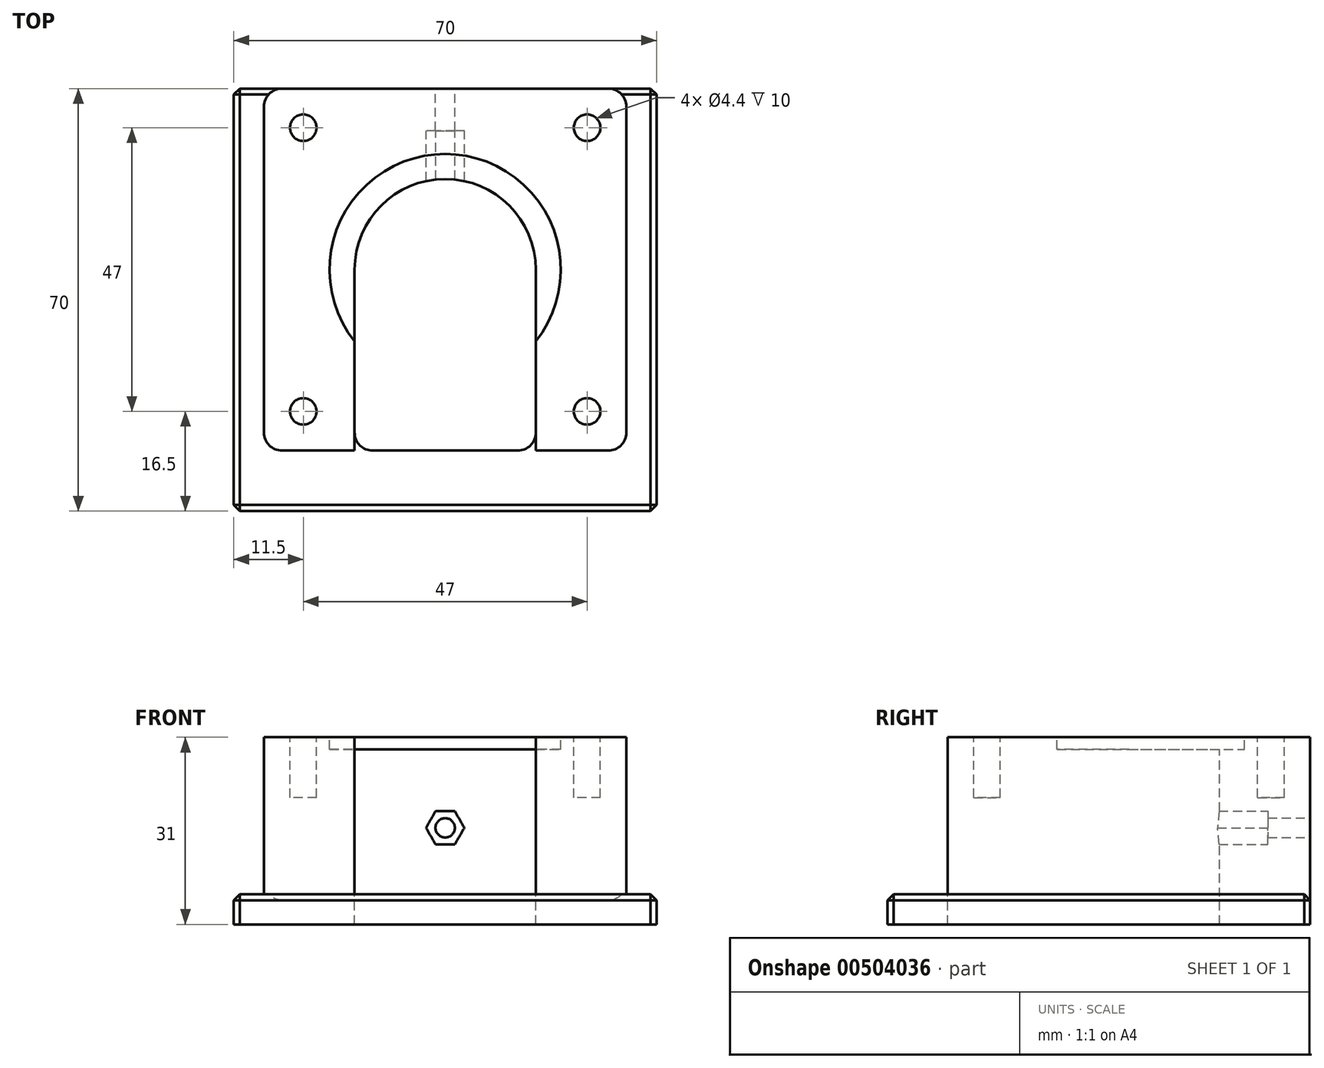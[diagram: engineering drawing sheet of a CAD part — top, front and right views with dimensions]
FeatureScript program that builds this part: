
annotation { "Feature Type Name" : "Feature", "Feature Type Description" : "" }
export const myFeature = defineFeature(function(context is Context, id is Id, definition is map)
    precondition{}
    {
        {
            var Q0;
            Q0=qCreatedBy(makeId("Top.planeOp"),FACE);
            var sketch = newSketch(context, id + "F0", { "sketchPlane" : qUnion([Q0])});
            skLineSegment(sketch, "E0.bottom", {"start": v(35, -35) * mm, "end": v(-35, -35) * mm});
            skLineSegment(sketch, "E0.top", {"start": v(35, 35) * mm, "end": v(-35, 35) * mm});
            skLineSegment(sketch, "E0.left", {"start": v(35, -35) * mm, "end": v(35, 35) * mm});
            skLineSegment(sketch, "E0.right", {"start": v(-35, -35) * mm, "end": v(-35, 35) * mm});
            skPoint(sketch, "E0.middle", {"position": v(0, 0) * mm});
            skSolve(sketch);
        }
        {
            var Q0;
            Q0=makeQuery(id+"F0.imprint","IMPRINT",FACE,{"disambiguationData":[TD([[makeQuery(id+"F0.imprint","IMPRINT",EDGE,{"derivedFrom":sQuery(id+"F0.wireOp",EDGE,"E0.bottom")}),-1.0]])]});
            extrude(context, id + "F1", {"entities" : qUnion([Q0]), "depth" : 5 * mm});
        }
        {
            var Q0;
            Q0=makeQuery(id+"F1.opExtrude","CAP_FACE",FACE,{"disambiguationData":[OSD([sQuery(id+"F0.wireOp",EDGE,"E0.bottom"),sQuery(id+"F0.wireOp",EDGE,"E0.top"),sQuery(id+"F0.wireOp",EDGE,"E0.left"),sQuery(id+"F0.wireOp",EDGE,"E0.right")])],"isStart":false});
            var sketch = newSketch(context, id + "F2", { "sketchPlane" : qUnion([Q0])});
            skLineSegment(sketch, "E1.bottom", {"start": v(30, -25) * mm, "end": v(-30, -25) * mm});
            skLineSegment(sketch, "E1.top", {"start": v(30, 35) * mm, "end": v(-30, 35) * mm});
            skLineSegment(sketch, "E1.left", {"start": v(30, -25) * mm, "end": v(30, 35) * mm});
            skLineSegment(sketch, "E1.right", {"start": v(-30, -25) * mm, "end": v(-30, 35) * mm});
            skPoint(sketch, "E1.middle", {"position": v(0, 5) * mm});
            skPoint(sketch, "E2", {"position": v(0, 35) * mm});
            skSolve(sketch);
        }
        {
            var Q0;
            Q0=makeQuery(id+"F2.imprint","IMPRINT",FACE,{"disambiguationData":[TD([[makeQuery(id+"F2.imprint","IMPRINT",EDGE,{"derivedFrom":sQuery(id+"F2.wireOp",EDGE,"E1.bottom")}),-1.0]])]});
            extrude(context, id + "F3", {"entities" : qUnion([Q0]), "operationType" : NewBodyOperationType.ADD, "depth" : 26 * mm});
        }
        {
            var Q0;
            Q0=makeQuery(id+"F3.opExtrude","CAP_FACE",FACE,{"disambiguationData":[OSD([sQuery(id+"F2.wireOp",EDGE,"E1.bottom"),sQuery(id+"F2.wireOp",EDGE,"E1.top"),sQuery(id+"F2.wireOp",EDGE,"E1.left"),sQuery(id+"F2.wireOp",EDGE,"E1.right")])],"isStart":false});
            var sketch = newSketch(context, id + "F4", { "sketchPlane" : qUnion([Q0])});
            skLineSegment(sketch, "E3.bottom", {"start": v(23.5, -18.5) * mm, "end": v(-23.5, -18.5) * mm, "construction": true});
            skLineSegment(sketch, "E3.top", {"start": v(23.5, 28.5) * mm, "end": v(-23.5, 28.5) * mm, "construction": true});
            skLineSegment(sketch, "E3.left", {"start": v(23.5, -18.5) * mm, "end": v(23.5, 28.5) * mm, "construction": true});
            skLineSegment(sketch, "E3.right", {"start": v(-23.5, -18.5) * mm, "end": v(-23.5, 28.5) * mm, "construction": true});
            skCircle(sketch, "E4", {"center": v(-23.5, 28.5) * mm, "radius": 2.2 * mm});
            skCircle(sketch, "E5", {"center": v(23.5, 28.5) * mm, "radius": 2.2 * mm});
            skCircle(sketch, "E6", {"center": v(-23.5, -18.5) * mm, "radius": 2.2 * mm});
            skCircle(sketch, "E7", {"center": v(23.5, -18.5) * mm, "radius": 2.2 * mm});
            skCircle(sketch, "E8", {"center": v(0, 5) * mm, "radius": 15 * mm});
            skLineSegment(sketch, "E9", {"start": v(-23.5, 28.5) * mm, "end": v(23.5, -18.5) * mm, "construction": true});
            skLineSegment(sketch, "E10", {"start": v(23.5, 28.5) * mm, "end": v(-23.5, -18.5) * mm, "construction": true});
            skLineSegment(sketch, "E11", {"start": v(15, 5) * mm, "end": v(15, -25) * mm});
            skLineSegment(sketch, "E12", {"start": v(-15, 5) * mm, "end": v(-15, -25) * mm});
            skLineSegment(sketch, "E13", {"start": v(-30, 35) * mm, "end": v(30, -25) * mm, "construction": true});
            skLineSegment(sketch, "E14", {"start": v(30, 35) * mm, "end": v(-30, -25) * mm, "construction": true});
            skCircle(sketch, "E15", {"center": v(0, 5) * mm, "radius": 19.15 * mm});
            skSolve(sketch);
        }
        {
            var Q0;
            Q0=makeQuery(id+"F4.imprint","IMPRINT",FACE,{"disambiguationData":[TD([[makeQuery(id+"F4.imprint","IMPRINT",EDGE,{"derivedFrom":sQuery(id+"F4.wireOp",EDGE,"E6")}),1.0]])]});
            var Q1;
            Q1=makeQuery(id+"F4.imprint","IMPRINT",FACE,{"disambiguationData":[TD([[makeQuery(id+"F4.imprint","IMPRINT",EDGE,{"derivedFrom":sQuery(id+"F4.wireOp",EDGE,"E4")}),1.0]])]});
            var Q2;
            Q2=makeQuery(id+"F4.imprint","IMPRINT",FACE,{"disambiguationData":[TD([[makeQuery(id+"F4.imprint","IMPRINT",EDGE,{"derivedFrom":sQuery(id+"F4.wireOp",EDGE,"E5")}),1.0]])]});
            var Q3;
            Q3=makeQuery(id+"F4.imprint","IMPRINT",FACE,{"disambiguationData":[TD([[makeQuery(id+"F4.imprint","IMPRINT",EDGE,{"derivedFrom":sQuery(id+"F4.wireOp",EDGE,"E7")}),1.0]])]});
            var Q4;
            Q4=makeQuery(id+"F1.opExtrude","CAP_FACE",FACE,{"disambiguationData":[OSD([sQuery(id+"F0.wireOp",EDGE,"E0.bottom"),sQuery(id+"F0.wireOp",EDGE,"E0.top"),sQuery(id+"F0.wireOp",EDGE,"E0.left"),sQuery(id+"F0.wireOp",EDGE,"E0.right")])],"isStart":true});
            extrude(context, id + "F5", {"entities" : qUnion([Q0, Q1, Q2, Q3]), "operationType" : NewBodyOperationType.REMOVE, "oppositeDirection" : true, "endBoundEntityFace" : qUnion([Q4]), "offsetDistance" : 25 * mm, "depth" : 10 * mm});
        }
        {
            var Q0;
            {var subQ0=sQuery(id+"F4.wireOp",EDGE,"E8");var subQ1=makeQuery(id+"F4.imprint","INTERSECT",VERTEX,{"derivedFrom":[subQ0,sQuery(id+"F4.wireOp",EDGE,"E11")]});Q0=makeQuery(id+"F4.imprint","IMPRINT",FACE,{"disambiguationData":[TD([[makeQuery(id+"F4.imprint","IMPRINT",EDGE,{"disambiguationData":[TD([[subQ1,-1.0]])],"derivedFrom":subQ0}),1.0]])]});}
            var Q1;
            {var subQ0=sQuery(id+"F4.wireOp",EDGE,"E11");var subQ1=sQuery(id+"F4.wireOp",EDGE,"E8");var subQ2=makeQuery(id+"F4.imprint","INTERSECT",VERTEX,{"derivedFrom":[subQ1,subQ0]});Q1=makeQuery(id+"F4.imprint","IMPRINT",FACE,{"disambiguationData":[TD([[makeQuery(id+"F4.imprint","IMPRINT",EDGE,{"disambiguationData":[TD([[subQ2,1.0]])],"derivedFrom":subQ1}),-1.0]])]});}
            var Q2;
            {var subQ0=sQuery(id+"F4.wireOp",EDGE,"E11");var subQ1=makeQuery(id+"F3.opExtrude","CAP_EDGE",EDGE,{"disambiguationData":[OSD([sQuery(id+"F2.wireOp",EDGE,"E1.bottom")])],"isStart":false});var subQ2=makeQuery(id+"F4.imprint","INTERSECT",VERTEX,{"derivedFrom":[subQ1,subQ0]});Q2=makeQuery(id+"F4.imprint","IMPRINT",FACE,{"disambiguationData":[TD([[makeQuery(id+"F4.imprint","IMPRINT",EDGE,{"disambiguationData":[TD([[subQ2,1.0]])],"derivedFrom":subQ0}),-1.0]])]});}
            extrude(context, id + "F6", {"entities" : qUnion([Q0, Q1, Q2]), "operationType" : NewBodyOperationType.REMOVE, "endBound" : BoundingType.THROUGH_ALL, "oppositeDirection" : true, "depth" : 25 * mm, "offsetDistance" : 25 * mm});
        }
        {
            var Q0;
            {var subQ0=sQuery(id+"F4.wireOp",EDGE,"E11");var subQ1=sQuery(id+"F4.wireOp",EDGE,"E8");var subQ2=makeQuery(id+"F4.imprint","INTERSECT",VERTEX,{"derivedFrom":[subQ1,subQ0]});Q0=makeQuery(id+"F4.imprint","IMPRINT",FACE,{"disambiguationData":[TD([[makeQuery(id+"F4.imprint","IMPRINT",EDGE,{"disambiguationData":[TD([[subQ2,-1.0]])],"derivedFrom":subQ1}),-1.0]])]});}
            extrude(context, id + "F7", {"entities" : qUnion([Q0]), "operationType" : NewBodyOperationType.REMOVE, "oppositeDirection" : true, "depth" : 2 * mm, "offsetDistance" : 25 * mm});
        }
        {
            var Q0;
            Q0=makeQuery(id+"F3.boolean.opBoolean","MERGE",FACE,{"derivedFrom":[makeQuery(id+"F1.opExtrude","SWEPT_FACE",FACE,{"disambiguationData":[OSD([sQuery(id+"F0.wireOp",EDGE,"E0.top")])]}),makeQuery(id+"F3.opExtrude","SWEPT_FACE",FACE,{"disambiguationData":[OSD([sQuery(id+"F2.wireOp",EDGE,"E1.top")])]})]});
            var sketch = newSketch(context, id + "F8", { "sketchPlane" : qUnion([Q0])});
            skLineSegment(sketch, "E16", {"start": v(-30, 16) * mm, "end": v(30, 16) * mm, "construction": true});
            skCircle(sketch, "E17", {"center": v(0, 16) * mm, "radius": 1.6 * mm});
            skCircle(sketch, "E18.cCircle", {"center": v(0, 16) * mm, "radius": 2.75 * mm, "construction": true});
            skLineSegment(sketch, "E18.0", {"start": v(1.59, 18.75) * mm, "end": v(3.18, 16) * mm});
            skLineSegment(sketch, "E18.1", {"start": v(3.18, 16) * mm, "end": v(1.59, 13.25) * mm});
            skLineSegment(sketch, "E18.2", {"start": v(1.59, 13.25) * mm, "end": v(-1.59, 13.25) * mm});
            skLineSegment(sketch, "E18.3", {"start": v(-1.59, 13.25) * mm, "end": v(-3.18, 16) * mm});
            skLineSegment(sketch, "E18.4", {"start": v(-3.18, 16) * mm, "end": v(-1.59, 18.75) * mm});
            skLineSegment(sketch, "E18.5", {"start": v(-1.59, 18.75) * mm, "end": v(1.59, 18.75) * mm});
            skPoint(sketch, "E18.0.midPoint", {"position": v(2.38, 17.37) * mm});
            skLineSegment(sketch, "E19", {"start": v(-3.18, 16) * mm, "end": v(3.18, 16) * mm, "construction": true});
            skSolve(sketch);
        }
        {
            var Q0;
            Q0=makeQuery(id+"F8.imprint","IMPRINT",FACE,{"disambiguationData":[TD([[makeQuery(id+"F8.imprint","IMPRINT",EDGE,{"derivedFrom":sQuery(id+"F8.wireOp",EDGE,"E17")}),1.0]])]});
            extrude(context, id + "F9", {"entities" : qUnion([Q0]), "operationType" : NewBodyOperationType.REMOVE, "endBound" : BoundingType.THROUGH_ALL, "oppositeDirection" : true, "depth" : 25 * mm});
        }
        {
            var Q0;
            Q0=makeQuery(id+"F8.imprint","IMPRINT",FACE,{"disambiguationData":[TD([[makeQuery(id+"F8.imprint","IMPRINT",EDGE,{"derivedFrom":sQuery(id+"F8.wireOp",EDGE,"E17")}),-1.0]])]});
            extrude(context, id + "F10", {"entities" : qUnion([Q0]), "operationType" : NewBodyOperationType.REMOVE, "oppositeDirection" : true, "depth" : 25 * mm, "hasSecondDirection" : true, "secondDirectionOppositeDirection" : true, "secondDirectionDepth" : 7 * mm});
        }
        {
            var Q0;
            Q0=makeQuery(id+"F3.opExtrude","SWEPT_EDGE",EDGE,{"disambiguationData":[OSD([sQuery(id+"F2.wireOp",EDGE,"E1.bottom"),sQuery(id+"F2.wireOp",EDGE,"E1.left")])]});
            var Q1;
            Q1=makeQuery(id+"F3.opExtrude","SWEPT_EDGE",EDGE,{"disambiguationData":[OSD([sQuery(id+"F2.wireOp",EDGE,"E1.bottom"),sQuery(id+"F2.wireOp",EDGE,"E1.right")])]});
            var Q2;
            Q2=makeQuery(id+"F3.opExtrude","SWEPT_EDGE",EDGE,{"disambiguationData":[OSD([sQuery(id+"F0.wireOp",EDGE,"E0.top"),sQuery(id+"F2.wireOp",EDGE,"E1.top"),sQuery(id+"F2.wireOp",EDGE,"E1.left")])]});
            var Q3;
            Q3=makeQuery(id+"F3.opExtrude","SWEPT_EDGE",EDGE,{"disambiguationData":[OSD([sQuery(id+"F0.wireOp",EDGE,"E0.top"),sQuery(id+"F2.wireOp",EDGE,"E1.top"),sQuery(id+"F2.wireOp",EDGE,"E1.right")])]});
            var Q4;
            {var subQ0=sQuery(id+"F2.wireOp",EDGE,"E1.bottom");var subQ1=sQuery(id+"F4.wireOp",EDGE,"E12");Q4=makeQuery(id+"F6.boolean.opBoolean","COPY",EDGE,{"disambiguationData":[topologyDisambiguationEdgeConnected([makeQuery(id+"F3.opExtrude","SWEPT_FACE",FACE,{"disambiguationData":[OSD([subQ0])]})])],"derivedFrom":makeQuery(id+"F6.opExtrude","SWEPT_EDGE",EDGE,{"disambiguationData":[OSD([subQ0,subQ1])]})});}
            var Q5;
            {var subQ0=sQuery(id+"F2.wireOp",EDGE,"E1.bottom");var subQ1=sQuery(id+"F4.wireOp",EDGE,"E11");Q5=makeQuery(id+"F6.boolean.opBoolean","COPY",EDGE,{"disambiguationData":[topologyDisambiguationEdgeConnected([makeQuery(id+"F3.opExtrude","SWEPT_FACE",FACE,{"disambiguationData":[OSD([subQ0])]})])],"derivedFrom":makeQuery(id+"F6.opExtrude","SWEPT_EDGE",EDGE,{"disambiguationData":[OSD([subQ0,subQ1])]})});}
            fillet(context, id + "F11", {"entities" : qUnion([Q0, Q1, Q2, Q3, Q4, Q5]), "radius" : 3 * mm, "tangentPropagation" : true, "allowEdgeOverflow" : false});
        }
        {
            var Q0;
            Q0=makeQuery(id+"F1.opExtrude","CAP_EDGE",EDGE,{"disambiguationData":[OSD([sQuery(id+"F0.wireOp",EDGE,"E0.right")])],"isStart":false});
            var Q1;
            Q1=makeQuery(id+"F1.opExtrude","CAP_EDGE",EDGE,{"disambiguationData":[OSD([sQuery(id+"F0.wireOp",EDGE,"E0.bottom")])],"isStart":false});
            var Q2;
            Q2=makeQuery(id+"F1.opExtrude","CAP_EDGE",EDGE,{"disambiguationData":[OSD([sQuery(id+"F0.wireOp",EDGE,"E0.left")])],"isStart":false});
            var Q3;
            {var subQ0=sQuery(id+"F0.wireOp",EDGE,"E0.left");var subQ1=sQuery(id+"F0.wireOp",EDGE,"E0.top");Q3=makeQuery(id+"F3.boolean.opBoolean","SPLIT",EDGE,{"disambiguationData":[TD([makeQuery(id+"F1.opExtrude","SWEPT_FACE",FACE,{"disambiguationData":[OSD([subQ0])]})])],"derivedFrom":makeQuery(id+"F1.opExtrude","CAP_EDGE",EDGE,{"disambiguationData":[OSD([subQ1])],"isStart":false})});}
            var Q4;
            {var subQ0=sQuery(id+"F0.wireOp",EDGE,"E0.right");var subQ1=sQuery(id+"F0.wireOp",EDGE,"E0.top");Q4=makeQuery(id+"F3.boolean.opBoolean","SPLIT",EDGE,{"disambiguationData":[TD([makeQuery(id+"F1.opExtrude","SWEPT_FACE",FACE,{"disambiguationData":[OSD([subQ0])]})])],"derivedFrom":makeQuery(id+"F1.opExtrude","CAP_EDGE",EDGE,{"disambiguationData":[OSD([subQ1])],"isStart":false})});}
            var Q5;
            Q5=makeQuery(id+"F1.opExtrude","SWEPT_EDGE",EDGE,{"disambiguationData":[OSD([sQuery(id+"F0.wireOp",EDGE,"E0.bottom"),sQuery(id+"F0.wireOp",EDGE,"E0.left")])]});
            var Q6;
            Q6=makeQuery(id+"F1.opExtrude","SWEPT_EDGE",EDGE,{"disambiguationData":[OSD([sQuery(id+"F0.wireOp",EDGE,"E0.bottom"),sQuery(id+"F0.wireOp",EDGE,"E0.right")])]});
            var Q7;
            Q7=makeQuery(id+"F1.opExtrude","SWEPT_EDGE",EDGE,{"disambiguationData":[OSD([sQuery(id+"F0.wireOp",EDGE,"E0.top"),sQuery(id+"F0.wireOp",EDGE,"E0.right")])]});
            var Q8;
            Q8=makeQuery(id+"F1.opExtrude","SWEPT_EDGE",EDGE,{"disambiguationData":[OSD([sQuery(id+"F0.wireOp",EDGE,"E0.top"),sQuery(id+"F0.wireOp",EDGE,"E0.left")])]});
            chamfer(context, id + "F12", {"entities" : qUnion([Q0, Q1, Q2, Q3, Q4, Q5, Q6, Q7, Q8]), "width" : 1 * mm, "tangentPropagation" : true});
        }
    });
